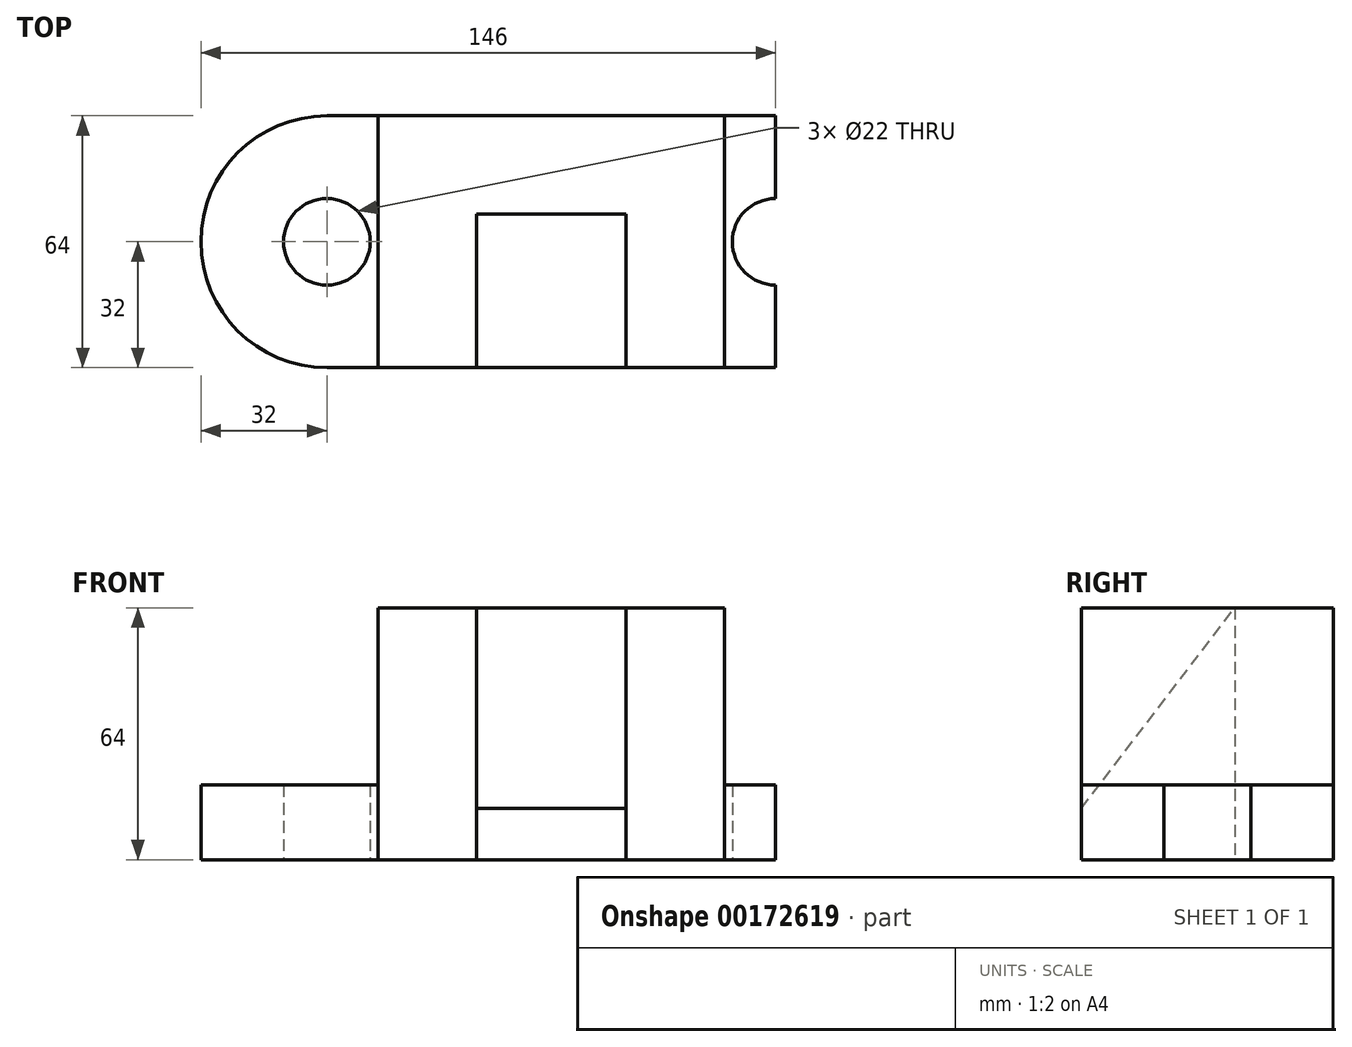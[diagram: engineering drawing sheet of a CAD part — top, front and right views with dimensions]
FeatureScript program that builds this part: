
annotation { "Feature Type Name" : "Feature", "Feature Type Description" : "" }
export const myFeature = defineFeature(function(context is Context, id is Id, definition is map)
    precondition{}
    {
        {
            var Q0;
            Q0=qCreatedBy(makeId("Top.planeOp"),FACE);
            var sketch = newSketch(context, id + "F0", { "sketchPlane" : qUnion([Q0])});
            skLineSegment(sketch, "E0.bottom", {"start": v(57, 32) * mm, "end": v(-57, 32) * mm});
            skLineSegment(sketch, "E0.top", {"start": v(57, -32) * mm, "end": v(-57, -32) * mm});
            skLineSegment(sketch, "E0.left", {"start": v(57, 32) * mm, "end": v(57, -32) * mm});
            skLineSegment(sketch, "E0.right", {"start": v(-57, 32) * mm, "end": v(-57, -32) * mm});
            skPoint(sketch, "E0.middle", {"position": v(0, 0) * mm});
            skArc(sketch, "E1", {"start": v(-57, 32) * mm, "mid": v(-89, 0) * mm, "end": v(-57, -32) * mm});
            skArc(sketch, "E2", {"start": v(57, 32) * mm, "mid": v(89, 0) * mm, "end": v(57, -32) * mm});
            skCircle(sketch, "E3", {"center": v(-57, 0) * mm, "radius": 11 * mm});
            skCircle(sketch, "E4", {"center": v(57, 0) * mm, "radius": 11 * mm});
            skLineSegment(sketch, "E5", {"start": v(-57, 0) * mm, "end": v(-44, 0) * mm, "construction": true});
            skLineSegment(sketch, "E6", {"start": v(-44, -32) * mm, "end": v(-44, 32) * mm});
            skLineSegment(sketch, "E7", {"start": v(57, 0) * mm, "end": v(44, 0) * mm, "construction": true});
            skLineSegment(sketch, "E8", {"start": v(44, -32) * mm, "end": v(44, 32) * mm});
            skLineSegment(sketch, "E9", {"start": v(-44, 0) * mm, "end": v(-19, 0) * mm, "construction": true});
            skLineSegment(sketch, "E10", {"start": v(44, 0) * mm, "end": v(19, 0) * mm, "construction": true});
            skLineSegment(sketch, "E11", {"start": v(0, 32) * mm, "end": v(0, 7) * mm, "construction": true});
            skPoint(sketch, "E11.endSnap0", {"position": v(0, 32) * mm});
            skLineSegment(sketch, "E12", {"start": v(-19, 7) * mm, "end": v(19, 7) * mm});
            skLineSegment(sketch, "E13", {"start": v(19, 7) * mm, "end": v(19, -32) * mm});
            skLineSegment(sketch, "E14", {"start": v(-19, 7) * mm, "end": v(-19, -32) * mm});
            skSolve(sketch);
        }
        {
            var Q0;
            {var subQ0=sQuery(id+"F0.wireOp",EDGE,"E1");Q0=makeQuery(id+"F0.imprint","IMPRINT",FACE,{"disambiguationData":[TD([[makeQuery(id+"F0.imprint","IMPRINT",EDGE,{"derivedFrom":subQ0}),1.0]])]});}
            var Q1;
            {var subQ9=sQuery(id+"F0.wireOp",EDGE,"E6");Q1=makeQuery(id+"F0.imprint","IMPRINT",FACE,{"disambiguationData":[TD([[makeQuery(id+"F0.imprint","IMPRINT",EDGE,{"derivedFrom":subQ9}),1.0]])]});}
            var Q2;
            {var subQ6=sQuery(id+"F0.wireOp",EDGE,"E8");Q2=makeQuery(id+"F0.imprint","IMPRINT",FACE,{"disambiguationData":[TD([[makeQuery(id+"F0.imprint","IMPRINT",EDGE,{"derivedFrom":subQ6}),-1.0]])]});}
            var Q3;
            {var subQ0=sQuery(id+"F0.wireOp",EDGE,"E2");Q3=makeQuery(id+"F0.imprint","IMPRINT",FACE,{"disambiguationData":[TD([[makeQuery(id+"F0.imprint","IMPRINT",EDGE,{"derivedFrom":subQ0}),-1.0]])]});}
            extrude(context, id + "F1", {"entities" : qUnion([Q0, Q1, Q2, Q3]), "depth" : 19 * mm});
        }
        {
            var Q0;
            {var subQ0=sQuery(id+"F0.wireOp",EDGE,"E6");Q0=makeQuery(id+"F0.imprint","IMPRINT",FACE,{"disambiguationData":[TD([[makeQuery(id+"F0.imprint","IMPRINT",EDGE,{"derivedFrom":subQ0}),-1.0]])]});}
            extrude(context, id + "F2", {"entities" : qUnion([Q0]), "depth" : 64 * mm});
        }
        {
            var Q0;
            Q0=makeQuery(id+"F2.opExtrude","SWEPT_FACE",FACE,{"disambiguationData":[OSD([sQuery(id+"F0.wireOp",EDGE,"E14")])]});
            var sketch = newSketch(context, id + "F3", { "sketchPlane" : qUnion([Q0])});
            skLineSegment(sketch, "E15", {"start": v(-32, 0) * mm, "end": v(-32, 13) * mm, "construction": true});
            skLineSegment(sketch, "E16", {"start": v(-32, 13) * mm, "end": v(7, 64) * mm});
            skSolve(sketch);
        }
        {
            var Q0;
            {var subQ0=sQuery(id+"F3.wireOp",EDGE,"E16");Q0=makeQuery(id+"F3.imprint","IMPRINT",FACE,{"disambiguationData":[TD([[makeQuery(id+"F3.imprint","IMPRINT",EDGE,{"derivedFrom":subQ0}),-1.0]])]});}
            extrude(context, id + "F4", {"entities" : qUnion([Q0]), "depth" : 38 * mm});
        }
    });
